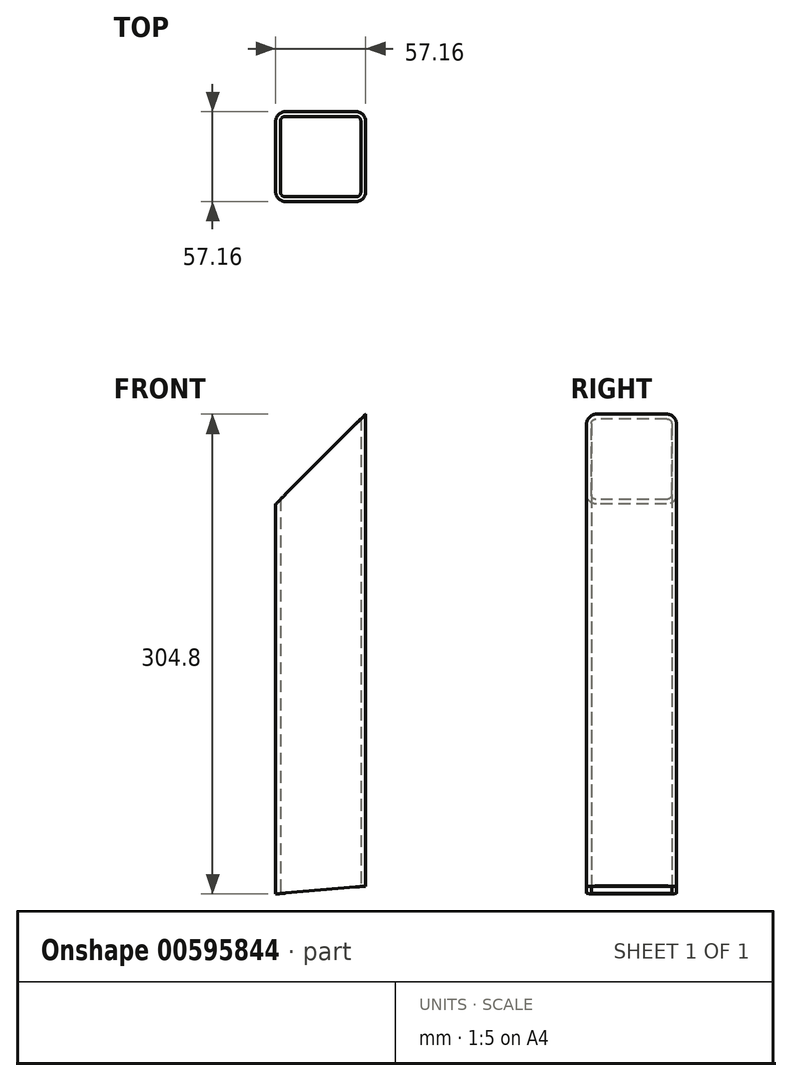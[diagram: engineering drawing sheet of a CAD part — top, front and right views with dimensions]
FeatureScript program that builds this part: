
annotation { "Feature Type Name" : "Feature", "Feature Type Description" : "" }
export const myFeature = defineFeature(function(context is Context, id is Id, definition is map)
    precondition{}
    {
        {
            var Q0;
            Q0=qCreatedBy(makeId("Top.planeOp"),FACE);
            var sketch = newSketch(context, id + "F0", { "sketchPlane" : qUnion([Q0])});
            skLineSegment(sketch, "E0.bottom", {"start": v(28.58, -28.58) * mm, "end": v(-28.58, -28.58) * mm});
            skLineSegment(sketch, "E0.top", {"start": v(28.58, 28.58) * mm, "end": v(-28.58, 28.58) * mm});
            skLineSegment(sketch, "E0.left", {"start": v(28.58, -28.58) * mm, "end": v(28.58, 28.58) * mm});
            skLineSegment(sketch, "E0.right", {"start": v(-28.57, -28.58) * mm, "end": v(-28.58, 28.58) * mm});
            skPoint(sketch, "E0.middle", {"position": v(0, 0) * mm});
            skLineSegment(sketch, "E1.bottom", {"start": v(-25.53, 25.53) * mm, "end": v(25.53, 25.53) * mm});
            skLineSegment(sketch, "E1.top", {"start": v(-25.53, -25.53) * mm, "end": v(25.53, -25.53) * mm});
            skLineSegment(sketch, "E1.left", {"start": v(-25.53, 25.53) * mm, "end": v(-25.53, -25.53) * mm});
            skLineSegment(sketch, "E1.right", {"start": v(25.53, 25.53) * mm, "end": v(25.53, -25.53) * mm});
            skSolve(sketch);
        }
        {
            var Q0;
            Q0=qSketchRegion(id+"F0",true);
            extrude(context, id + "F1", {"entities" : qUnion([Q0]), "depth" : 304.8 * mm, "offsetDistance" : 25.4 * mm});
        }
        {
            var Q0;
            Q0=makeQuery(id+"F1.opExtrude","SWEPT_EDGE",EDGE,{"disambiguationData":[OSD([sQuery(id+"F0.wireOp",EDGE,"E1.bottom"),sQuery(id+"F0.wireOp",EDGE,"E1.right")])]});
            var Q1;
            Q1=makeQuery(id+"F1.opExtrude","SWEPT_EDGE",EDGE,{"disambiguationData":[OSD([sQuery(id+"F0.wireOp",EDGE,"E1.bottom"),sQuery(id+"F0.wireOp",EDGE,"E1.left")])]});
            var Q2;
            Q2=makeQuery(id+"F1.opExtrude","SWEPT_EDGE",EDGE,{"disambiguationData":[OSD([sQuery(id+"F0.wireOp",EDGE,"E1.top"),sQuery(id+"F0.wireOp",EDGE,"E1.left")])]});
            var Q3;
            Q3=makeQuery(id+"F1.opExtrude","SWEPT_EDGE",EDGE,{"disambiguationData":[OSD([sQuery(id+"F0.wireOp",EDGE,"E1.top"),sQuery(id+"F0.wireOp",EDGE,"E1.right")])]});
            fillet(context, id + "F2", {"entities" : qUnion([Q0, Q1, Q2, Q3]), "radius" : 3.05 * mm, "tangentPropagation" : true, "allowEdgeOverflow" : false});
        }
        {
            var Q0;
            Q0=makeQuery(id+"F1.opExtrude","SWEPT_EDGE",EDGE,{"disambiguationData":[OSD([sQuery(id+"F0.wireOp",EDGE,"E0.top"),sQuery(id+"F0.wireOp",EDGE,"E0.right")])]});
            var Q1;
            Q1=makeQuery(id+"F1.opExtrude","SWEPT_EDGE",EDGE,{"disambiguationData":[OSD([sQuery(id+"F0.wireOp",EDGE,"E0.bottom"),sQuery(id+"F0.wireOp",EDGE,"E0.right")])]});
            var Q2;
            Q2=makeQuery(id+"F1.opExtrude","SWEPT_EDGE",EDGE,{"disambiguationData":[OSD([sQuery(id+"F0.wireOp",EDGE,"E0.bottom"),sQuery(id+"F0.wireOp",EDGE,"E0.left")])]});
            var Q3;
            Q3=makeQuery(id+"F1.opExtrude","SWEPT_EDGE",EDGE,{"disambiguationData":[OSD([sQuery(id+"F0.wireOp",EDGE,"E0.top"),sQuery(id+"F0.wireOp",EDGE,"E0.left")])]});
            fillet(context, id + "F3", {"entities" : qUnion([Q0, Q1, Q2, Q3]), "radius" : 6.35 * mm, "tangentPropagation" : true, "allowEdgeOverflow" : false});
        }
        {
            var Q0;
            Q0=qCreatedBy(makeId("Front.planeOp"),FACE);
            var sketch = newSketch(context, id + "F4", { "sketchPlane" : qUnion([Q0])});
            skLineSegment(sketch, "E2", {"start": v(28.58, 304.8) * mm, "end": v(-28.58, 247.65) * mm});
            skLineSegment(sketch, "E3", {"start": v(-28.58, 247.65) * mm, "end": v(-28.58, 304.8) * mm});
            skLineSegment(sketch, "E4", {"start": v(-28.58, 304.8) * mm, "end": v(28.57, 304.8) * mm});
            skLineSegment(sketch, "E5", {"start": v(28.57, 304.8) * mm, "end": v(28.57, 304.8) * mm});
            skSolve(sketch);
        }
        {
            var Q0;
            Q0=qSketchRegion(id+"F4",true);
            extrude(context, id + "F5", {"entities" : qUnion([Q0]), "operationType" : NewBodyOperationType.REMOVE, "endBound" : BoundingType.THROUGH_ALL, "oppositeDirection" : true, "depth" : 25.4 * mm, "offsetDistance" : 25.4 * mm, "hasSecondDirection" : true, "secondDirectionBound" : SecondDirectionBoundingType.THROUGH_ALL, "secondDirectionOppositeDirection" : false, "secondDirectionDepth" : 25.4 * mm});
        }
        {
            var Q0;
            Q0=qCreatedBy(makeId("Front.planeOp"),FACE);
            var sketch = newSketch(context, id + "F6", { "sketchPlane" : qUnion([Q0])});
            skLineSegment(sketch, "E6", {"start": v(-28.58, 0) * mm, "end": v(28.58, 5) * mm});
            skLineSegment(sketch, "E7", {"start": v(28.58, 5) * mm, "end": v(28.58, 0) * mm});
            skLineSegment(sketch, "E8", {"start": v(-28.58, 0) * mm, "end": v(28.58, 0) * mm});
            skSolve(sketch);
        }
        {
            var Q0;
            Q0 = qSketchRegion(id + "F6", true);
            extrude(context, id + "F7", {"entities" : qUnion([Q0]), "operationType" : NewBodyOperationType.REMOVE, "endBound" : BoundingType.THROUGH_ALL, "oppositeDirection" : true, "depth" : 25.4 * mm, "offsetDistance" : 25.4 * mm, "hasSecondDirection" : true, "secondDirectionBound" : SecondDirectionBoundingType.THROUGH_ALL, "secondDirectionOppositeDirection" : false, "secondDirectionDepth" : 25.4 * mm});
        }
    });
